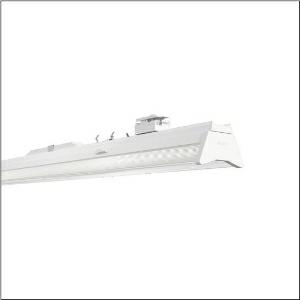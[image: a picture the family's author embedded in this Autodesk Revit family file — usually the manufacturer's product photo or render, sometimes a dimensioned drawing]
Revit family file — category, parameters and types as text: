
# Revit family: licross_r__21_performance_mo_51td16vn375g_e9bb
name_source: partatom
category: Lighting Fixtures
units: mm (PartAtom-declared; Revit-internal decimal feet)

## family parameters
Cut with Voids When Loaded = No
Host = Face
Light Source = No
Part Type = Normal
Room Calculation Point = No
Round Connector Dimension = Use Diameter
Shared = No

## types (1)
- --- (1 x LED, 7700 lm, 44.1 W, 3000K)
    Apparent Load = 44 VA
    CIE Flux Codes = 66 88 96 79 100
    Color Rendering = 80
    Color Temperature = 3000K
    Default Elevation = 1800 mm
    Description = Licross® 21 Performance MO, luminaire insert, of sheet steel, galvanised, coil coated, white, length: 1.500mm, width: 120mm, height: 123mm, LED rated luminous flux: 7.700lm, light colour: 830, control gear: DALI 2, CLO, with plug, 5-pole, with phase selection, mains connection: 220..240V, AC, 50/60Hz, start of lifetime: 44W, end of service life: 49W, internal wiring halogen-free, primary light control with lens, of plastic, primary optical cover: cover, of PMMA, light emission: direct/indirect distribution, primary light characteristic: symmetric, protection rating (complete): IP54, insulation class (complete): insulation class I (protective earthing), certification: CE, ENEC, VDE, UKCA, protection symbol: D if used in an environment with non-conductive dust loads with corresponding accessories, impact resistance: IK06, permissible ambient temperature for indoor applications: -25..+35°C, corresponds to IFS (International Featured Standards) requirements for safety and quality in the food industry, reducing of maximum allowable ambient temperature of 5°C with ceiling mounting, LABS conformity tested according to VDMA 24364:2018-05, packaging unit: 1 piece
    Height = 114 mm
    Lamp = 1 x LED
    Lamp Light Flux = 7700 lm
    Lamp Power = 44.1 W
    Lamp count = 1
    Length = 1500 mm
    Luminous efficacy = 175 lm/W
    Manufacturer = Siteco
    ModVariant = No
    Model = 51TD16VN375G
    Mounting Place = Ceiling
    Mounting Type = Pendant
    Number of Poles = 1
    OnlyDefault = Yes
    Power Factor = 1
    Product Name = Licross® 21 Performance MO
    Product group = luminaire insert | ceiling pendant
    ProductGroupID = 902
    Protection Class = Protection class I
    Protection Degree = IP 54
    RLX_Detail_Level = 1
    RLX_Emergency_Light_Flux = 0 lm
    RLX_Emergency_Type = 0
    RLX_Emergency_Type_DB = No
    RlxData = <blob elided: 34085 chars, md5=131692dd>
    Socket = socket
    Standby Power = 0 W
    System Light Flux = 7700 lm
    System Power = 44 W
    Type Comments = factory setting: luminous flux: 100 % | dim-lin: 254 | 294 mA
    Type Image = l_1256138.jpg
    URL = http://relux.com
    VarID = @adj_004225
    Voltage = 0 V
    Weight = 0.00 kg
    Width = 120 mm

## geometry (parser evidence)
native form markers: Blend x4, Sweep x13
no freeform markers — native parametric forms only
